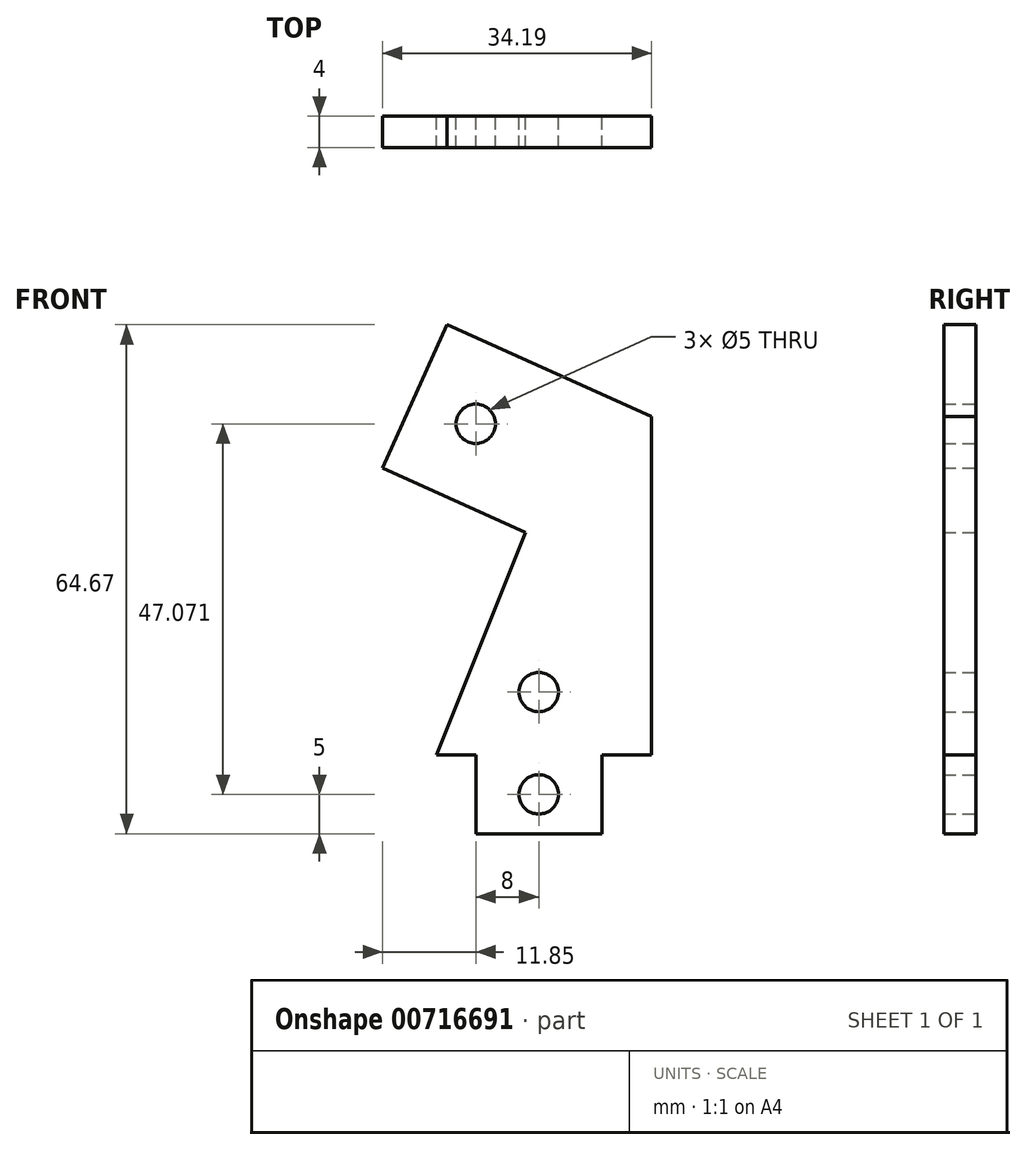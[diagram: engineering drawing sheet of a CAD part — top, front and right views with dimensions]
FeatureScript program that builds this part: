
annotation { "Feature Type Name" : "Feature", "Feature Type Description" : "" }
export const myFeature = defineFeature(function(context is Context, id is Id, definition is map)
    precondition{}
    {
        {
            var Q0;
            Q0=qCreatedBy(makeId("Front.planeOp"),FACE);
            var sketch = newSketch(context, id + "F0", { "sketchPlane" : qUnion([Q0])});
            skLineSegment(sketch, "E0.bottom", {"start": v(0, 0) * mm, "end": v(16, 0) * mm});
            skLineSegment(sketch, "E0.left", {"start": v(0, 0) * mm, "end": v(0, 10) * mm});
            skLineSegment(sketch, "E0.right", {"start": v(16, 0) * mm, "end": v(16, 10) * mm});
            skCircle(sketch, "E1", {"center": v(8, 5) * mm, "radius": 2.5 * mm});
            skLineSegment(sketch, "E2", {"start": v(0, 10) * mm, "end": v(-5, 10) * mm});
            skLineSegment(sketch, "E3", {"start": v(-5, 10) * mm, "end": v(6.34, 38.26) * mm});
            skLineSegment(sketch, "E4", {"start": v(6.34, 38.26) * mm, "end": v(-11.85, 46.43) * mm});
            skLineSegment(sketch, "E5", {"start": v(-11.85, 46.43) * mm, "end": v(-3.66, 64.67) * mm});
            skLineSegment(sketch, "E6", {"start": v(-3.66, 64.67) * mm, "end": v(22.34, 53) * mm});
            skLineSegment(sketch, "E7", {"start": v(22.34, 53) * mm, "end": v(22.34, 10) * mm});
            skLineSegment(sketch, "E8", {"start": v(22.34, 10) * mm, "end": v(16, 10) * mm});
            skCircle(sketch, "E9", {"center": v(8, 18) * mm, "radius": 2.5 * mm});
            skCircle(sketch, "E10", {"center": v(0, 52.07) * mm, "radius": 2.5 * mm});
            skSolve(sketch);
        }
        {
            var Q0;
            Q0=makeQuery(id+"F0.imprint","IMPRINT",FACE,{"disambiguationData":[TD([[makeQuery(id+"F0.imprint","IMPRINT",EDGE,{"derivedFrom":sQuery(id+"F0.wireOp",EDGE,"E0.bottom")}),1.0]])]});
            extrude(context, id + "F1", {"entities" : qUnion([Q0]), "depth" : 4 * mm, "offsetDistance" : 25 * mm});
        }
    });
